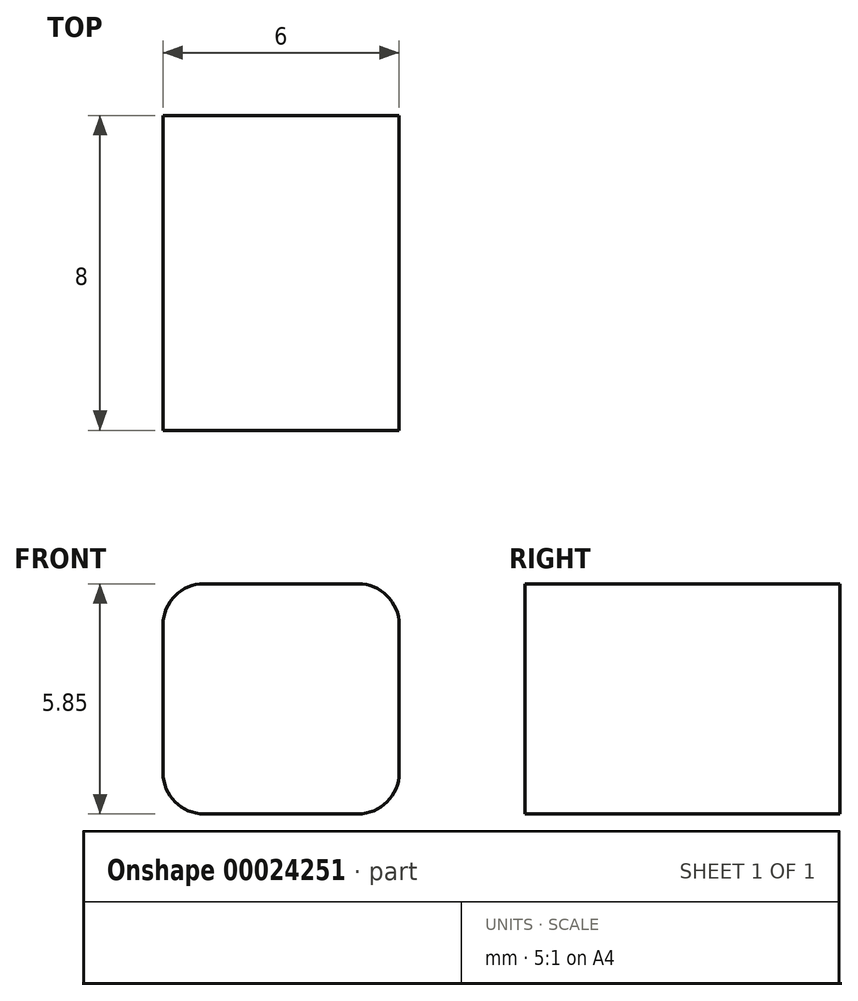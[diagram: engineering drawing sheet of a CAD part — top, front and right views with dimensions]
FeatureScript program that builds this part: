
annotation { "Feature Type Name" : "Feature", "Feature Type Description" : "" }
export const myFeature = defineFeature(function(context is Context, id is Id, definition is map)
    precondition{}
    {
        {
            var Q0;
            Q0=qCreatedBy(makeId("Front.planeOp"),FACE);
            var sketch = newSketch(context, id + "F0", { "sketchPlane" : qUnion([Q0])});
            skLineSegment(sketch, "E0.rect.bottom", {"start": v(-1.96, -2.29) * mm, "end": v(1.96, -2.29) * mm});
            skLineSegment(sketch, "E0.rect.top", {"start": v(-1.96, 3.56) * mm, "end": v(1.96, 3.56) * mm});
            skLineSegment(sketch, "E0.rect.left", {"start": v(-3, -1.24) * mm, "end": v(-3, 2.52) * mm});
            skLineSegment(sketch, "E0.rect.right", {"start": v(3, -1.24) * mm, "end": v(3, 2.52) * mm});
            skPoint(sketch, "E0.rect.middle", {"position": v(0, 0.64) * mm});
            skPoint(sketch, "E1.visualSharp", {"position": v(3, 3.56) * mm});
            skArc(sketch, "E1.filletArc", {"start": v(3, 2.52) * mm, "mid": v(2.7, 3.26) * mm, "end": v(1.96, 3.56) * mm});
            skPoint(sketch, "E2.visualSharp", {"position": v(3, -2.29) * mm});
            skArc(sketch, "E2.filletArc", {"start": v(1.96, -2.29) * mm, "mid": v(2.7, -1.98) * mm, "end": v(3, -1.24) * mm});
            skPoint(sketch, "E3.visualSharp", {"position": v(-3, 3.56) * mm});
            skArc(sketch, "E3.filletArc", {"start": v(-1.96, 3.56) * mm, "mid": v(-2.7, 3.26) * mm, "end": v(-3, 2.52) * mm});
            skPoint(sketch, "E4.visualSharp", {"position": v(-3, -2.29) * mm});
            skArc(sketch, "E4.filletArc", {"start": v(-3, -1.24) * mm, "mid": v(-2.7, -1.98) * mm, "end": v(-1.96, -2.29) * mm});
            skSolve(sketch);
        }
        {
            var Q0;
            Q0=makeQuery(id+"F0.imprint","IMPRINT",FACE,{"disambiguationData":[TD([[makeQuery(id+"F0.imprint","IMPRINT",EDGE,{"derivedFrom":sQuery(id+"F0.wireOp",EDGE,"E0.rect.bottom")}),1.0]])]});
            extrude(context, id + "F1", {"entities" : qUnion([Q0]), "depth" : 8 * mm});
        }
    });
